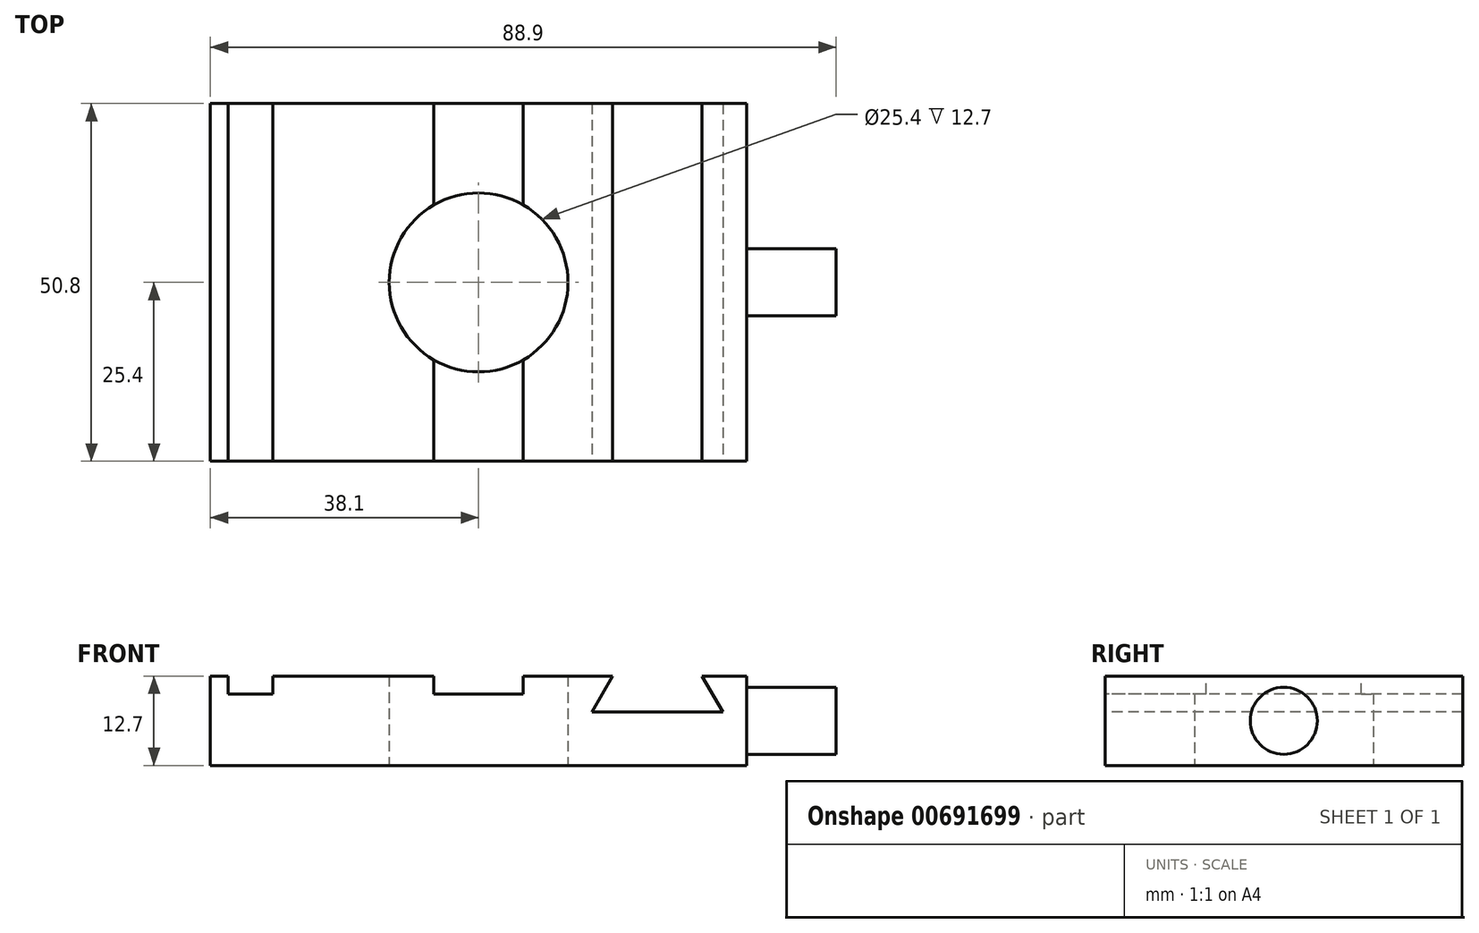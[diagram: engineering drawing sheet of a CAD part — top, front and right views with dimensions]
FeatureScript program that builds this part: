
annotation { "Feature Type Name" : "Feature", "Feature Type Description" : "" }
export const myFeature = defineFeature(function(context is Context, id is Id, definition is map)
    precondition{}
    {
        {
            var Q0;
            Q0=qCreatedBy(makeId("Top.planeOp"),FACE);
            var sketch = newSketch(context, id + "F0", { "sketchPlane" : qUnion([Q0])});
            skLineSegment(sketch, "E0.bottom", {"start": v(-38.1, 25.4) * mm, "end": v(38.1, 25.4) * mm});
            skLineSegment(sketch, "E0.top", {"start": v(-38.1, -25.4) * mm, "end": v(38.1, -25.4) * mm});
            skLineSegment(sketch, "E0.left", {"start": v(-38.1, 25.4) * mm, "end": v(-38.1, -25.4) * mm});
            skLineSegment(sketch, "E0.right", {"start": v(38.1, 25.4) * mm, "end": v(38.1, -25.4) * mm});
            skPoint(sketch, "E0.middle", {"position": v(0, 0) * mm});
            skCircle(sketch, "E1", {"center": v(0, 0) * mm, "radius": 12.7 * mm});
            skSolve(sketch);
        }
        {
            var Q0;
            Q0=makeQuery(id+"F0.imprint","IMPRINT",FACE,{"disambiguationData":[TD([[makeQuery(id+"F0.imprint","IMPRINT",EDGE,{"derivedFrom":sQuery(id+"F0.wireOp",EDGE,"E0.bottom")}),-1.0]])]});
            extrude(context, id + "F1", {"entities" : qUnion([Q0]), "depth" : 12.7 * mm, "offsetDistance" : 25.4 * mm});
        }
        {
            var Q0;
            Q0=makeQuery(id+"F1.opExtrude","CAP_FACE",FACE,{"disambiguationData":[OSD([sQuery(id+"F0.wireOp",EDGE,"E0.bottom"),sQuery(id+"F0.wireOp",EDGE,"E0.top"),sQuery(id+"F0.wireOp",EDGE,"E0.left"),sQuery(id+"F0.wireOp",EDGE,"E0.right"),sQuery(id+"F0.wireOp",EDGE,"E1")])],"isStart":false});
            var sketch = newSketch(context, id + "F2", { "sketchPlane" : qUnion([Q0])});
            skLineSegment(sketch, "E2.bottom", {"start": v(-35.56, 25.4) * mm, "end": v(-29.2, 25.4) * mm});
            skLineSegment(sketch, "E2.top", {"start": v(-35.56, -25.4) * mm, "end": v(-29.2, -25.4) * mm});
            skLineSegment(sketch, "E2.left", {"start": v(-35.56, 25.4) * mm, "end": v(-35.56, -25.4) * mm});
            skLineSegment(sketch, "E2.right", {"start": v(-29.2, 25.4) * mm, "end": v(-29.2, -25.4) * mm});
            skLineSegment(sketch, "E3", {"start": v(-6.35, 25.4) * mm, "end": v(-6.35, -25.4) * mm});
            skLineSegment(sketch, "E4", {"start": v(-6.35, -25.4) * mm, "end": v(6.35, -25.4) * mm});
            skLineSegment(sketch, "E5", {"start": v(6.35, -25.4) * mm, "end": v(6.35, 25.4) * mm});
            skLineSegment(sketch, "E6", {"start": v(6.35, 25.4) * mm, "end": v(-6.35, 25.4) * mm});
            skLineSegment(sketch, "E7", {"start": v(0, 25.4) * mm, "end": v(0, -25.4) * mm, "construction": true});
            skSolve(sketch);
        }
        {
            var Q0;
            Q0=makeQuery(id+"F2.imprint","IMPRINT",FACE,{"disambiguationData":[TD([[makeQuery(id+"F2.imprint","IMPRINT",EDGE,{"derivedFrom":sQuery(id+"F2.wireOp",EDGE,"E2.bottom")}),-1.0]])]});
            var Q1;
            {var subQ0=sQuery(id+"F2.wireOp",EDGE,"E4");Q1=makeQuery(id+"F2.imprint","IMPRINT",FACE,{"disambiguationData":[TD([[makeQuery(id+"F2.imprint","IMPRINT",EDGE,{"derivedFrom":subQ0}),1.0]])]});}
            var Q2;
            {var subQ0=sQuery(id+"F2.wireOp",EDGE,"E6");Q2=makeQuery(id+"F2.imprint","IMPRINT",FACE,{"disambiguationData":[TD([[makeQuery(id+"F2.imprint","IMPRINT",EDGE,{"derivedFrom":subQ0}),-1.0]])]});}
            extrude(context, id + "F3", {"entities" : qUnion([Q0, Q1, Q2]), "operationType" : NewBodyOperationType.REMOVE, "oppositeDirection" : true, "depth" : 2.54 * mm, "offsetDistance" : 25.4 * mm});
        }
        {
            var Q0;
            Q0=makeQuery(id+"F1.opExtrude","SWEPT_FACE",FACE,{"disambiguationData":[OSD([sQuery(id+"F0.wireOp",EDGE,"E0.top")])]});
            var sketch = newSketch(context, id + "F4", { "sketchPlane" : qUnion([Q0])});
            skLineSegment(sketch, "E8", {"start": v(19.05, 12.7) * mm, "end": v(16.12, 7.62) * mm});
            skLineSegment(sketch, "E9", {"start": v(16.12, 7.62) * mm, "end": v(34.68, 7.62) * mm});
            skLineSegment(sketch, "E10", {"start": v(34.68, 7.62) * mm, "end": v(31.75, 12.7) * mm});
            skLineSegment(sketch, "E11", {"start": v(31.75, 12.7) * mm, "end": v(19.05, 12.7) * mm});
            skLineSegment(sketch, "E12", {"start": v(25.4, 7.62) * mm, "end": v(25.4, 12.7) * mm, "construction": true});
            skSolve(sketch);
        }
        {
            var Q0;
            Q0=makeQuery(id+"F4.imprint","IMPRINT",FACE,{"disambiguationData":[TD([[makeQuery(id+"F4.imprint","IMPRINT",EDGE,{"derivedFrom":sQuery(id+"F4.wireOp",EDGE,"E8")}),1.0]])]});
            extrude(context, id + "F5", {"entities" : qUnion([Q0]), "operationType" : NewBodyOperationType.REMOVE, "endBound" : BoundingType.THROUGH_ALL, "oppositeDirection" : true, "depth" : 25.4 * mm, "offsetDistance" : 25.4 * mm});
        }
        {
            var Q0;
            Q0=makeQuery(id+"F1.opExtrude","SWEPT_FACE",FACE,{"disambiguationData":[OSD([sQuery(id+"F0.wireOp",EDGE,"E0.right")])]});
            var sketch = newSketch(context, id + "F6", { "sketchPlane" : qUnion([Q0])});
            skCircle(sketch, "E13", {"center": v(0, 6.35) * mm, "radius": 4.76 * mm});
            skPoint(sketch, "E13.centerSnap0", {"position": v(-25.4, 6.35) * mm});
            skPoint(sketch, "E13.centerSnap1", {"position": v(0, 12.7) * mm});
            skSolve(sketch);
        }
        {
            var Q0;
            Q0 = qSketchRegion(id + "F6", true);
            extrude(context, id + "F7", {"entities" : qUnion([Q0]), "operationType" : NewBodyOperationType.ADD, "depth" : 12.7 * mm, "offsetDistance" : 25.4 * mm});
        }
    });
